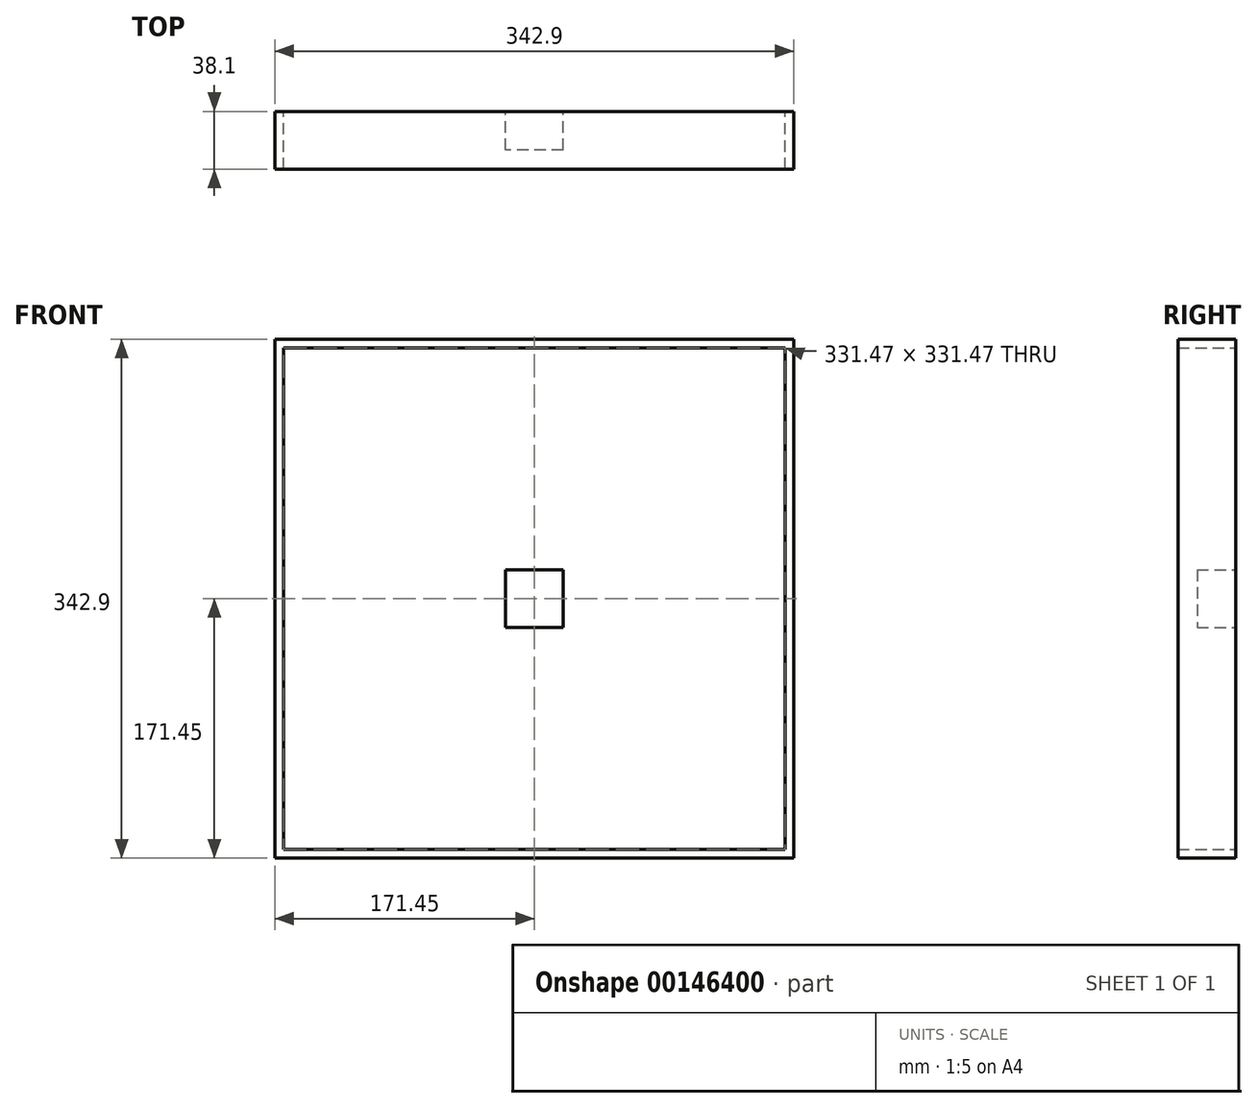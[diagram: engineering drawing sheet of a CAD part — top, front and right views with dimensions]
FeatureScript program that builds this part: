
annotation { "Feature Type Name" : "Feature", "Feature Type Description" : "" }
export const myFeature = defineFeature(function(context is Context, id is Id, definition is map)
    precondition{}
    {
        {
            var Q0;
            Q0=qCreatedBy(makeId("Front.planeOp"),FACE);
            var sketch = newSketch(context, id + "F0", { "sketchPlane" : qUnion([Q0])});
            skLineSegment(sketch, "E0.bottom", {"start": v(171.45, 171.45) * mm, "end": v(-171.45, 171.45) * mm});
            skLineSegment(sketch, "E0.top", {"start": v(171.45, -171.45) * mm, "end": v(-171.45, -171.45) * mm});
            skLineSegment(sketch, "E0.left", {"start": v(171.45, 171.45) * mm, "end": v(171.45, -171.45) * mm});
            skLineSegment(sketch, "E0.right", {"start": v(-171.45, 171.45) * mm, "end": v(-171.45, -171.45) * mm});
            skPoint(sketch, "E0.middle", {"position": v(0, 0) * mm});
            skLineSegment(sketch, "E1.bottom", {"start": v(165.74, 165.73) * mm, "end": v(-165.74, 165.73) * mm});
            skLineSegment(sketch, "E1.top", {"start": v(165.74, -165.74) * mm, "end": v(-165.74, -165.74) * mm});
            skLineSegment(sketch, "E1.left", {"start": v(165.73, 165.74) * mm, "end": v(165.74, -165.74) * mm});
            skLineSegment(sketch, "E1.right", {"start": v(-165.74, 165.73) * mm, "end": v(-165.74, -165.74) * mm});
            skLineSegment(sketch, "E2.bottom", {"start": v(19.05, 165.73) * mm, "end": v(-19.05, 165.73) * mm});
            skLineSegment(sketch, "E2.top", {"start": v(19.05, -165.73) * mm, "end": v(-19.05, -165.73) * mm});
            skLineSegment(sketch, "E2.left", {"start": v(19.05, 165.74) * mm, "end": v(19.05, -165.74) * mm});
            skLineSegment(sketch, "E2.right", {"start": v(-19.05, 165.74) * mm, "end": v(-19.05, -165.74) * mm});
            skLineSegment(sketch, "E3.bottom", {"start": v(165.74, 19.05) * mm, "end": v(-165.74, 19.05) * mm});
            skLineSegment(sketch, "E3.top", {"start": v(165.74, -19.05) * mm, "end": v(-165.74, -19.05) * mm});
            skLineSegment(sketch, "E3.left", {"start": v(165.74, 19.05) * mm, "end": v(165.74, -19.05) * mm});
            skLineSegment(sketch, "E3.right", {"start": v(-165.74, 19.05) * mm, "end": v(-165.74, -19.05) * mm});
            skLineSegment(sketch, "E4.bottom", {"start": v(-165.74, 165.73) * mm, "end": v(-127.64, 165.73) * mm});
            skLineSegment(sketch, "E4.top", {"start": v(-165.74, 127.64) * mm, "end": v(-127.64, 127.64) * mm});
            skLineSegment(sketch, "E4.left", {"start": v(-165.74, 165.73) * mm, "end": v(-165.74, 127.64) * mm});
            skLineSegment(sketch, "E4.right", {"start": v(-127.64, 165.73) * mm, "end": v(-127.64, 127.64) * mm});
            skLineSegment(sketch, "E5.bottom", {"start": v(-165.74, -165.74) * mm, "end": v(-127.64, -165.74) * mm});
            skLineSegment(sketch, "E5.top", {"start": v(-165.74, -127.64) * mm, "end": v(-127.64, -127.64) * mm});
            skLineSegment(sketch, "E5.left", {"start": v(-165.74, -165.74) * mm, "end": v(-165.74, -127.64) * mm});
            skLineSegment(sketch, "E5.right", {"start": v(-127.64, -165.74) * mm, "end": v(-127.64, -127.64) * mm});
            skLineSegment(sketch, "E6.bottom", {"start": v(165.74, 165.73) * mm, "end": v(127.64, 165.73) * mm});
            skLineSegment(sketch, "E6.top", {"start": v(165.74, 127.64) * mm, "end": v(127.64, 127.64) * mm});
            skLineSegment(sketch, "E6.left", {"start": v(165.74, 165.73) * mm, "end": v(165.74, 127.64) * mm});
            skLineSegment(sketch, "E6.right", {"start": v(127.64, 165.73) * mm, "end": v(127.64, 127.64) * mm});
            skLineSegment(sketch, "E7.bottom", {"start": v(165.74, -165.74) * mm, "end": v(127.64, -165.74) * mm});
            skLineSegment(sketch, "E7.top", {"start": v(165.74, -127.64) * mm, "end": v(127.64, -127.64) * mm});
            skLineSegment(sketch, "E7.left", {"start": v(165.74, -165.74) * mm, "end": v(165.74, -127.64) * mm});
            skLineSegment(sketch, "E7.right", {"start": v(127.64, -165.74) * mm, "end": v(127.64, -127.64) * mm});
            skSolve(sketch);
        }
        {
            var Q0;
            Q0=makeQuery(id+"F0.imprint","IMPRINT",FACE,{"disambiguationData":[TD([[makeQuery(id+"F0.imprint","IMPRINT",EDGE,{"derivedFrom":sQuery(id+"F0.wireOp",EDGE,"E0.bottom")}),1.0]])]});
            extrude(context, id + "F1", {"entities" : qUnion([Q0]), "depth" : 38.1 * mm});
        }
        {
            var Q0;
            {var subQ0=sQuery(id+"F0.wireOp",EDGE,"E2.bottom");Q0=makeQuery(id+"F0.imprint","IMPRINT",FACE,{"disambiguationData":[TD([[makeQuery(id+"F0.imprint","IMPRINT",EDGE,{"derivedFrom":subQ0}),1.0]])]});}
            var Q1;
            Q1=makeQuery(id+"F0.imprint","IMPRINT",FACE,{"disambiguationData":[TD([[makeQuery(id+"F0.imprint","IMPRINT",EDGE,{"derivedFrom":sQuery(id+"F0.wireOp",EDGE,"E7.bottom")}),-1.0]])]});
            var Q2;
            {var subQ0=sQuery(id+"F0.wireOp",EDGE,"E3.bottom");var subQ1=sQuery(id+"F0.wireOp",EDGE,"E2.left");var subQ2=makeQuery(id+"F0.imprint","INTERSECT",VERTEX,{"derivedFrom":[subQ1,subQ0]});Q2=makeQuery(id+"F0.imprint","IMPRINT",FACE,{"disambiguationData":[TD([[makeQuery(id+"F0.imprint","IMPRINT",EDGE,{"disambiguationData":[TD([[subQ2,-1.0]])],"derivedFrom":subQ1}),-1.0]])]});}
            var Q3;
            Q3=makeQuery(id+"F0.imprint","IMPRINT",FACE,{"disambiguationData":[TD([[makeQuery(id+"F0.imprint","IMPRINT",EDGE,{"derivedFrom":sQuery(id+"F0.wireOp",EDGE,"E6.bottom")}),1.0]])]});
            var Q4;
            {var subQ5=sQuery(id+"F0.wireOp",EDGE,"E3.right");Q4=makeQuery(id+"F0.imprint","IMPRINT",FACE,{"disambiguationData":[TD([[makeQuery(id+"F0.imprint","IMPRINT",EDGE,{"derivedFrom":subQ5}),1.0]])]});}
            var Q5;
            {var subQ5=sQuery(id+"F0.wireOp",EDGE,"E3.left");Q5=makeQuery(id+"F0.imprint","IMPRINT",FACE,{"disambiguationData":[TD([[makeQuery(id+"F0.imprint","IMPRINT",EDGE,{"derivedFrom":subQ5}),-1.0]])]});}
            var Q6;
            Q6=makeQuery(id+"F0.imprint","IMPRINT",FACE,{"disambiguationData":[TD([[makeQuery(id+"F0.imprint","IMPRINT",EDGE,{"derivedFrom":sQuery(id+"F0.wireOp",EDGE,"E5.bottom")}),1.0]])]});
            var Q7;
            {var subQ0=sQuery(id+"F0.wireOp",EDGE,"E2.top");Q7=makeQuery(id+"F0.imprint","IMPRINT",FACE,{"disambiguationData":[TD([[makeQuery(id+"F0.imprint","IMPRINT",EDGE,{"derivedFrom":subQ0}),-1.0]])]});}
            var Q8;
            Q8=makeQuery(id+"F0.imprint","IMPRINT",FACE,{"disambiguationData":[TD([[makeQuery(id+"F0.imprint","IMPRINT",EDGE,{"derivedFrom":sQuery(id+"F0.wireOp",EDGE,"E4.bottom")}),-1.0]])]});
            extrude(context, id + "F2", {"entities" : qUnion([Q0, Q1, Q2, Q3, Q4, Q5, Q6, Q7, Q8]), "operationType" : NewBodyOperationType.ADD, "depth" : 25.4 * mm});
        }
    });
